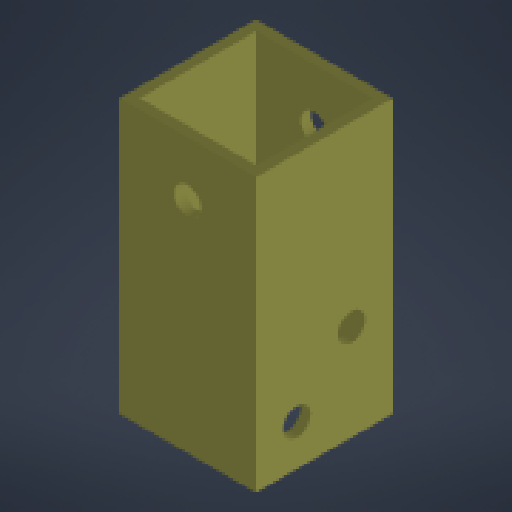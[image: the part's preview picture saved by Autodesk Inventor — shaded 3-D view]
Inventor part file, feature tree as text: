
AUTODESK INVENTOR PART (.ipt)
format: ipt  version: 2024 (Build 280153000, 153)  size: 159,744 bytes
history: native  units: mm
features: other x8, reference x6, extrude x3, sketch x3
ambient origin geometry x8: Origin, YZ Plane, XZ Plane, XY Plane, X Axis, Y Axis, Z Axis, Center Point
bodies: Body1 (feature_tree)
feature tree (20):
  other  "Твердое тело1"
  other  "РабПлоскость1"
  extrude  "Выдавливание1"  Depth=1.5mm
  other  "РабПлоскость2"
  extrude  "Выдавливание2"  Depth=40.0mm TaperAngle=0.0deg
  extrude  "Выдавливание3"  TaperAngle=0.0deg  [1 undecoded]
  sketch  "Эскиз1"
  reference  "Ссылка1"
  reference  "Ссылка2"
  reference  "Ссылка3"
  sketch  "Эскиз2"
  reference  "Ссылка4"
  reference  "Ссылка5"
  sketch  "Эскиз3"
  reference  "Ссылка6"
  parser-record x1  (decoder bookkeeping rows leaked as tree rows — omitted from the tree; the rows remain in map.json)
  other  "base_assembly.iam"
  other  "square_box_section:1"
  other  "plate:1"
  other  "plate:2"
note: 1 required parameter value undecoded (feature->parameter linkage not recoverable at this tier; creation-order binding heuristic only, values carry confidence <= 0.55)
note: 1 file-system path scrubbed to <path> (originals preserved in map.json)
